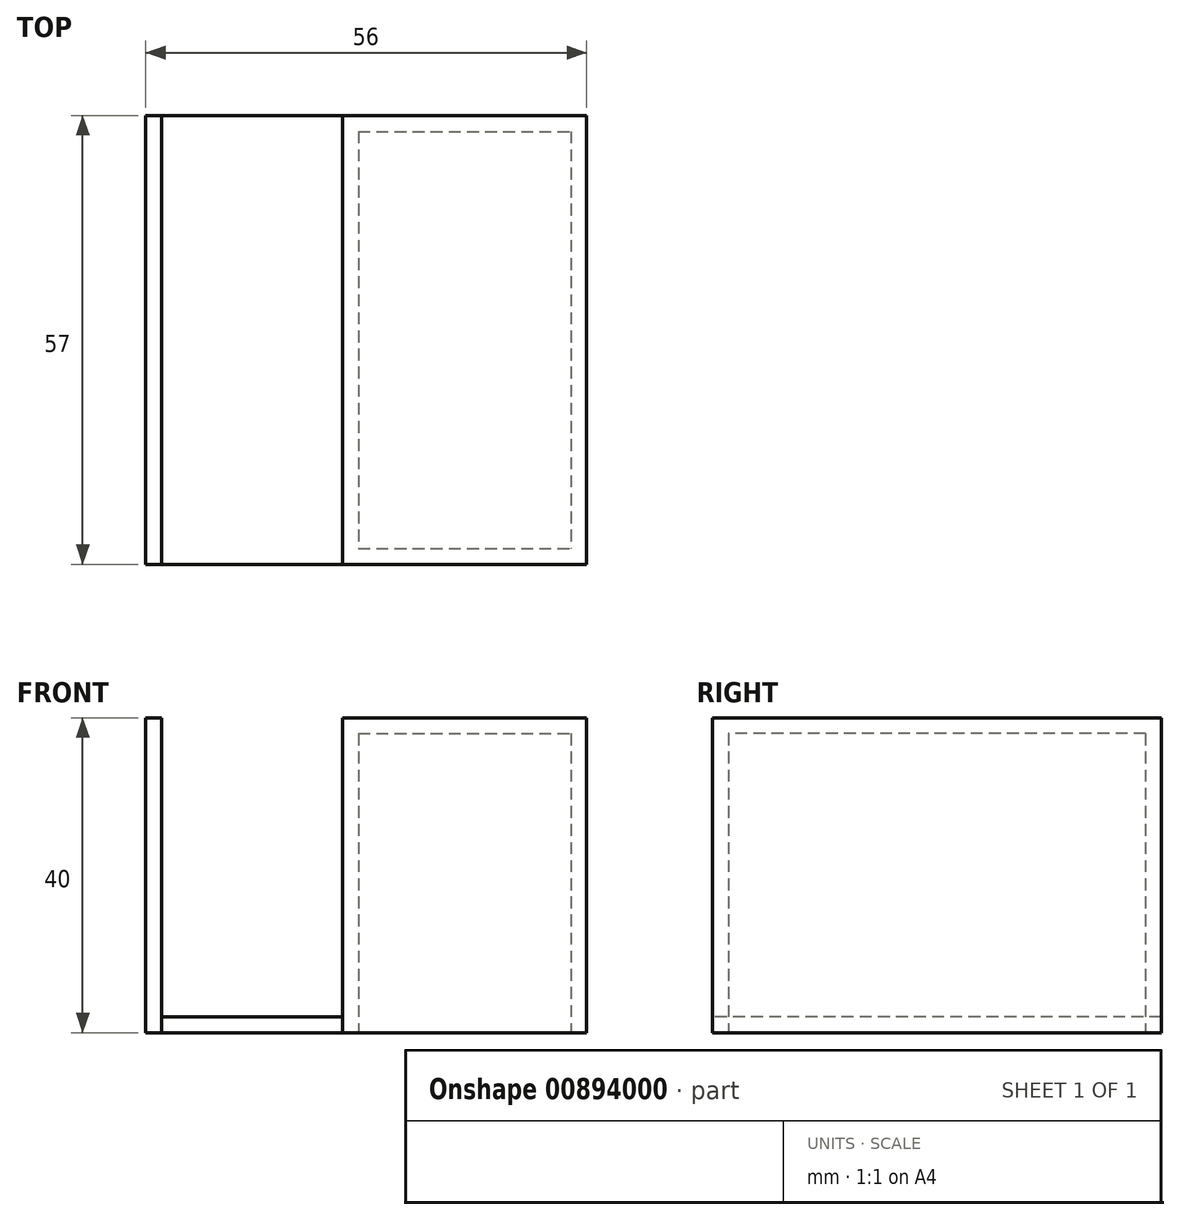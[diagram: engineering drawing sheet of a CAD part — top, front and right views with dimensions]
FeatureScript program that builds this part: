
annotation { "Feature Type Name" : "Feature", "Feature Type Description" : "" }
export const myFeature = defineFeature(function(context is Context, id is Id, definition is map)
    precondition{}
    {
        {
            var Q0;
            Q0=qCreatedBy(makeId("Top.planeOp"),FACE);
            var sketch = newSketch(context, id + "F0", { "sketchPlane" : qUnion([Q0])});
            skLineSegment(sketch, "E0.bottom", {"start": v(-2.84, 47.28) * mm, "end": v(53.16, 47.28) * mm});
            skLineSegment(sketch, "E0.top", {"start": v(-2.84, -9.72) * mm, "end": v(53.16, -9.72) * mm});
            skLineSegment(sketch, "E0.left", {"start": v(-2.84, 47.28) * mm, "end": v(-2.84, -9.72) * mm});
            skLineSegment(sketch, "E0.right", {"start": v(53.16, 47.28) * mm, "end": v(53.16, -9.72) * mm});
            skLineSegment(sketch, "E1.bottom", {"start": v(24.16, 45.28) * mm, "end": v(51.16, 45.28) * mm});
            skLineSegment(sketch, "E1.top", {"start": v(24.16, -7.72) * mm, "end": v(51.16, -7.72) * mm});
            skLineSegment(sketch, "E1.left", {"start": v(24.16, 45.28) * mm, "end": v(24.16, -7.72) * mm});
            skLineSegment(sketch, "E1.right", {"start": v(51.16, 45.28) * mm, "end": v(51.16, -7.72) * mm});
            skLineSegment(sketch, "E2", {"start": v(22.16, 47.28) * mm, "end": v(22.16, -9.72) * mm});
            skLineSegment(sketch, "E3", {"start": v(-0.84, 47.28) * mm, "end": v(-0.84, -9.72) * mm});
            skSolve(sketch);
        }
        {
            var Q0;
            {var subQ0=sQuery(id+"F0.wireOp",EDGE,"E0.left");Q0=makeQuery(id+"F0.imprint","IMPRINT",FACE,{"disambiguationData":[TD([[makeQuery(id+"F0.imprint","IMPRINT",EDGE,{"derivedFrom":subQ0}),1.0]])]});}
            var Q1;
            {var subQ0=sQuery(id+"F0.wireOp",EDGE,"E0.right");Q1=makeQuery(id+"F0.imprint","IMPRINT",FACE,{"disambiguationData":[TD([[makeQuery(id+"F0.imprint","IMPRINT",EDGE,{"derivedFrom":subQ0}),-1.0]])]});}
            extrude(context, id + "F1", {"entities" : qUnion([Q0, Q1]), "depth" : 40 * mm, "offsetDistance" : 25 * mm});
        }
        {
            var Q0;
            {var subQ0=sQuery(id+"F0.wireOp",EDGE,"E2");Q0=makeQuery(id+"F0.imprint","IMPRINT",FACE,{"disambiguationData":[TD([[makeQuery(id+"F0.imprint","IMPRINT",EDGE,{"derivedFrom":subQ0}),-1.0]])]});}
            extrude(context, id + "F2", {"entities" : qUnion([Q0]), "depth" : 2 * mm, "offsetDistance" : 25 * mm});
        }
        {
            var Q0;
            Q0=makeQuery(id+"F0.imprint","IMPRINT",FACE,{"disambiguationData":[TD([[makeQuery(id+"F0.imprint","IMPRINT",EDGE,{"derivedFrom":sQuery(id+"F0.wireOp",EDGE,"E1.bottom")}),-1.0]])]});
            extrude(context, id + "F3", {"entities" : qUnion([Q0]), "operationType" : NewBodyOperationType.ADD, "depth" : 40 * mm, "offsetDistance" : 25 * mm});
        }
        {
            var Q0;
            Q0=makeQuery(id+"F0.imprint","IMPRINT",FACE,{"disambiguationData":[TD([[makeQuery(id+"F0.imprint","IMPRINT",EDGE,{"derivedFrom":sQuery(id+"F0.wireOp",EDGE,"E1.bottom")}),-1.0]])]});
            extrude(context, id + "F4", {"entities" : qUnion([Q0]), "operationType" : NewBodyOperationType.REMOVE, "depth" : 38 * mm, "offsetDistance" : 25 * mm});
        }
    });
